# Revit family: QF_BOURGEAT_HARMONIE_2TVO_Modèles_hauteur_rabaisée_primaire
name_source: partatom
category: Equipement spécialisé
revit_build: Autodesk Revit 2015 (Build: 20140606_1530(x64)
units: mm (PartAtom-declared; Revit-internal decimal feet)

## types (3) — shared parameters
Décalage du sol = 27 mm  [stored 0.0885827 ft]
Fabricant = BOURGEAT
Hauteur hors tout = 1007 mm  [stored 3.30381 ft]
Hauteur plan de travail = 680 mm  [stored 2.23097 ft]
Hauteur porte = 563 mm  [stored 1.84711 ft]
Inox = Acier inoxydable, poli
Longueur hors tout = 1061 mm  [stored 3.48097 ft]
Pieds = Oui
Poids net à vide = 55.00 kg
Profondeur hors tout = 761 mm  [stored 2.49672 ft]
Roulettes = Non
Spécification du Fabricant = Table de tri harmonie
URL catalogue = http://www.bourgeat.fr
Vert = Vert

## per-type parameters (varying)
| type | Modèle | Panneau arrière | Panneau avant | Portes arrière | Portes avant |
| Modèle sur pieds - sans portes | 859202 | Oui | Non | Non | Non |
| Modèle sur pieds - portes arrière | 859212 | Non | Oui | Oui | Non |
| Modèle sur pieds - portes avant | 859222 | Oui | Non | Non | Oui |

note: [stored X ft] marks values corroborated as IEEE doubles in the binary element streams (Revit-internal decimal feet)

## geometry (parser evidence)
native form markers: Blend x8
no freeform markers — native parametric forms only
